# Revit family: 6451000918
name_source: partatom
category: Plumbing Fixtures
units: mm (PartAtom-declared; Revit-internal decimal feet)

## family parameters
Always vertical = Yes
Cut with Voids When Loaded = No
OmniClass Number = 23.45.55.00
OmniClass Title = Sanitary Faucets, Wastes
Part Type = Normal
Room Calculation Point = No
Round Connector Dimension = Use Diameter
Shared = No
Work Plane-Based = No

## types (1)
- 6451000918 Data unit, Bluetooth
    2D/3D/BIM Files URL = http://static.hansa.com
    3D View = https://static.hansa.com
    Additional Features = Minimum required water flow 1.5l/min
    Approval ABP = PA-IX 062/I
    Approval KIWA SE Type Approval = 1820
    AssetType = Fixed
    BIMObjectName = 6451000918
    Bluetooth = 5.x (D060576)
    BodyMaterial = Brass
    Brand = HANSA
    Catalog Drawing URL = http://static.hansa.com
    CloseOffRating = 0
    Color = Anthracite grey
    Connection = Internal thread
    Connection Size = G3/8
    Default Elevation = 0 mm  [stored 0 ft]
    Dimension Drawing URL = http://static.hansa.com
    DurationUnit = Year
    EAN Number = 4057304016974
    EMC Directive = Radio Equipment Directive 2014/53/EU , 
Low Voltage Directive 2014/35/EU , 
EMC Directive 2014/30/EU , 
RoHS Directive 2011/65/EU
    ETIM Class Number = EC002580
    FDV Document URL = http://www.hansa.com
    FaucetMainMaterial = Brass
    Features = Self-powered;Bluetooth®
    Finish = Polished
    Flow Drawing URL = http://static.hansa.com
    Flow Rate At 300kPa = 0.2 L/s
    FlowCoefficient = 0
    Group = Smart accessory
    IfcExportAs = IfcValveType
    IfcExportType = FAUCET
    InletConnectionSize = 16 mm  [stored 0.0524934 ft]
    Installation Type = Wall mounted
    Installation and Maintenance Guide URL = http://static.hansa.com
    Interactive AR View URL = https://static.hansa.com
    Manufacturer = HANSA
    ManufacturerName = HANSA
    ManufacturerURL = http://www.hansa.com
    Market = International;Germany
    Material = Composite
    Max. Hot Water Supply = 70 °C
    Mechanical Parts = Litter filter(s)
    Mobile Product Information URL = http://mpi.hansa.com
    Model = 6451000918 Data unit, Bluetooth
    ModelReference = 6451000918
    NBSDescription = Water supply fittings for wash basins and troughs
    NBSReference = 45-35-70/371
    Name = 6451000918 Data unit, Bluetooth
    Name_en = 6451000918 Data unit, Bluetooth
    Noise Class = I (ISO 3822)
    NominalDepth = 68 mm
    NominalHeight = 122 mm
    NominalWidth = 56 mm
    Operating Voltage = 0 V
    Pressure Loss With Flow 01ls = 87000.0 Pa
    Product Code = 6451000918
    Product Family = HANSAELECTRA
    Product Image URL = http://static.hansa.com
    Product URL = http://static.hansa.com
    Protection Class = IP 55
    Sales Package dimensions (LxWxH) = 164 x 85 x 85
    Shape = Sculptured
    Size = 55x70x125 mm
    Spare-Part Information URL = http://static.hansa.com
    Surface treatment = Anthracite grey
    Technical DataSheet URL = http://www.hansa.com
    UNSPSC Class Number = 30181800 Faucet and shower heads, jets and parts and accessories
    URL ABP = http://static.hansa.com
    URL Declaration Of Performance (DOP) = http://static.hansa.com
    URL Declaration of Asbestos = http://static.hansa.com
    URL Declaration of Conformity = http://static.hansa.com
    URL Declaration of SCIP = http://static.hansa.com
    URL EU Packaging Declaration = http://static.hansa.com
    URL EcoLabel Declaration = http://static.hansa.com
    URL KIWA SE Type Approval = http://static.hansa.com
    URL Materials Declaration = http://www.hansa.com
    URL REACH = http://static.hansa.com
    URL WEEE = http://static.hansa.com
    Uniclass2 = Pr_40_30_96_96
    Uniclass2015Description = Washbasin manual water supply sets
    Uniclass2015Reference = Pr_40_20_87_96
    ValveMainMaterial = Fine Textured - Anthracite grey
    Version = 1
    VersionDate = 01/06/2023
    Warranty Information URL = http://warranty.hansa.com
    WarrantyDescription = http://warranty.hansa.com
    WarrantyDurationUnit = Year
    Working Pressure = 100 - 1000 kPa

note: [stored X ft] marks values corroborated as IEEE doubles in the binary element streams (Revit-internal decimal feet)

## geometry (parser evidence)
native form markers: Sweep x4
no freeform markers — native parametric forms only
